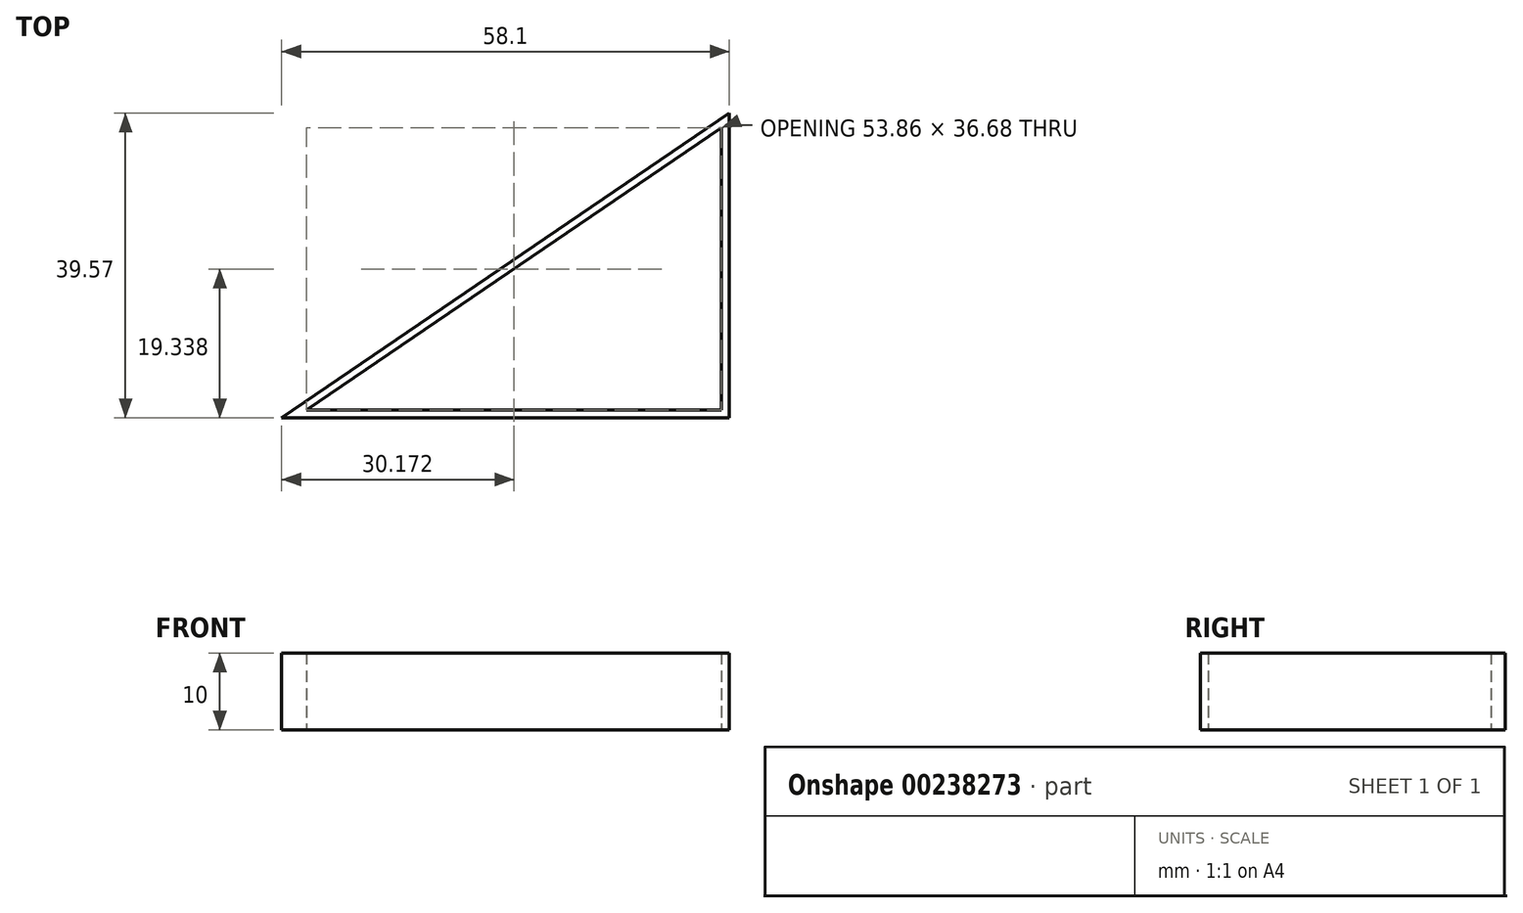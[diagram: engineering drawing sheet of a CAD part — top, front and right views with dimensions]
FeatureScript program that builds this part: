
annotation { "Feature Type Name" : "Feature", "Feature Type Description" : "" }
export const myFeature = defineFeature(function(context is Context, id is Id, definition is map)
    precondition{}
    {
        {
            var Q0;
            Q0=qCreatedBy(makeId("Top.planeOp"),FACE);
            var sketch = newSketch(context, id + "F0", { "sketchPlane" : qUnion([Q0])});
            skLineSegment(sketch, "E0", {"start": v(0, 0) * mm, "end": v(-58.1, 0) * mm});
            skLineSegment(sketch, "E1", {"start": v(0, 0) * mm, "end": v(0, 39.57) * mm});
            skLineSegment(sketch, "E2", {"start": v(0, 39.57) * mm, "end": v(-58.1, 0) * mm});
            skLineSegment(sketch, "E3.0", {"start": v(-1, 37.68) * mm, "end": v(-54.86, 1) * mm});
            skLineSegment(sketch, "E3.1", {"start": v(-1, 1) * mm, "end": v(-1, 37.68) * mm});
            skLineSegment(sketch, "E3.2", {"start": v(-1, 1) * mm, "end": v(-54.86, 1) * mm});
            skSolve(sketch);
        }
        {
            var Q0;
            Q0=makeQuery(id+"F0.imprint","IMPRINT",FACE,{"disambiguationData":[TD([[makeQuery(id+"F0.imprint","IMPRINT",EDGE,{"derivedFrom":sQuery(id+"F0.wireOp",EDGE,"E0")}),-1.0]])]});
            extrude(context, id + "F1", {"entities" : qUnion([Q0]), "depth" : 10 * mm});
        }
    });
